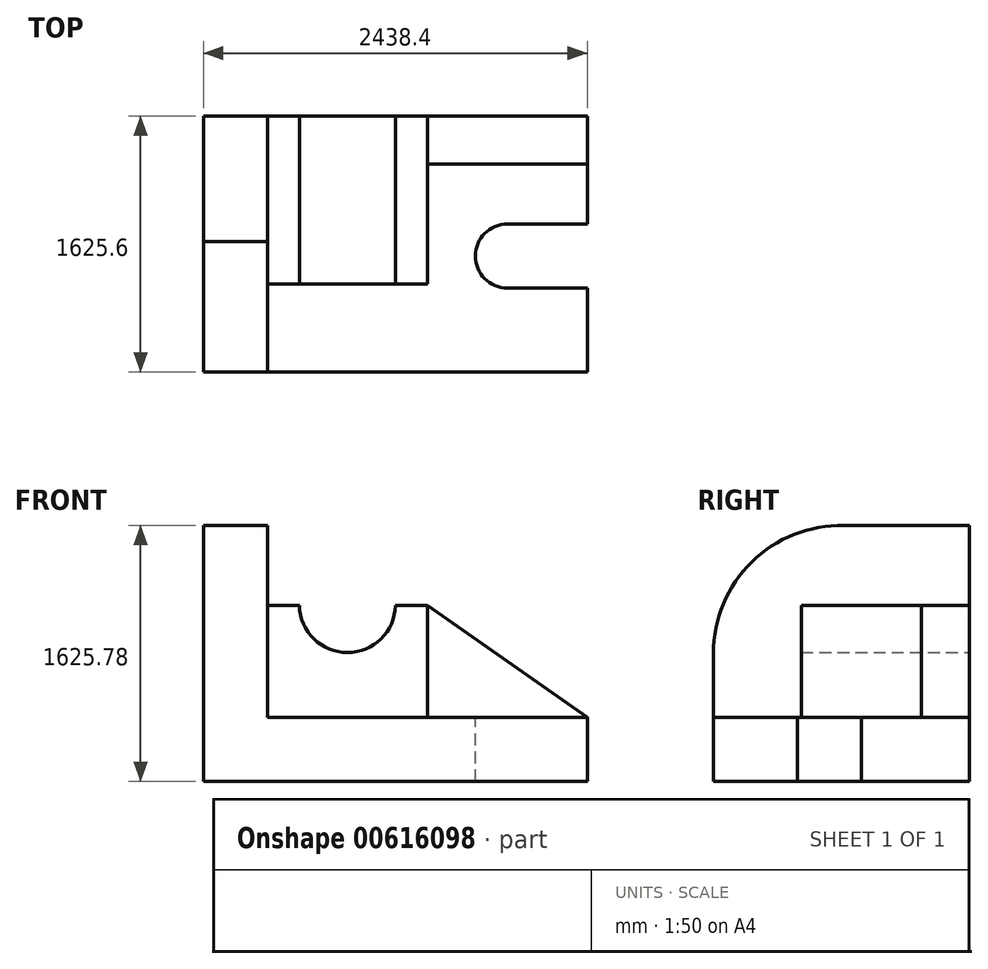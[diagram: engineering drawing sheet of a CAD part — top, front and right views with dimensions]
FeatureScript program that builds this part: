
annotation { "Feature Type Name" : "Feature", "Feature Type Description" : "" }
export const myFeature = defineFeature(function(context is Context, id is Id, definition is map)
    precondition{}
    {
        {
            var Q0;
            Q0=qCreatedBy(makeId("Top.planeOp"),FACE);
            var sketch = newSketch(context, id + "F0", { "sketchPlane" : qUnion([Q0])});
            skLineSegment(sketch, "E0.bottom", {"start": v(-2382.66, 1583.48) * mm, "end": v(55.74, 1583.48) * mm});
            skLineSegment(sketch, "E0.top", {"start": v(-2382.66, -42.12) * mm, "end": v(55.74, -42.12) * mm});
            skLineSegment(sketch, "E0.left", {"start": v(-2382.66, 1583.48) * mm, "end": v(-2382.66, -42.12) * mm});
            skLineSegment(sketch, "E0.right", {"start": v(55.74, 1583.48) * mm, "end": v(55.74, -42.12) * mm});
            skSolve(sketch);
        }
        {
            var Q0;
            Q0=makeQuery(id+"F0.imprint","IMPRINT",FACE,{"disambiguationData":[TD([[makeQuery(id+"F0.imprint","IMPRINT",EDGE,{"derivedFrom":sQuery(id+"F0.wireOp",EDGE,"E0.bottom")}),-1.0]])]});
            extrude(context, id + "F1", {"entities" : qUnion([Q0]), "depth" : 406.4 * mm, "offsetDistance" : 25.4 * mm});
        }
        {
            var Q0;
            Q0=makeQuery(id+"F1.opExtrude","SWEPT_FACE",FACE,{"disambiguationData":[OSD([sQuery(id+"F0.wireOp",EDGE,"E0.left")])]});
            var sketch = newSketch(context, id + "F2", { "sketchPlane" : qUnion([Q0])});
            skLineSegment(sketch, "E1", {"start": v(-1583.48, 0) * mm, "end": v(42.12, 0) * mm});
            skLineSegment(sketch, "E2", {"start": v(42.12, 0) * mm, "end": v(42.12, 812.98) * mm});
            skArc(sketch, "E3", {"start": v(42.12, 812.98) * mm, "mid": v(-202.01, 1393.72) * mm, "end": v(-787.76, 1625.6) * mm});
            skLineSegment(sketch, "E4", {"start": v(-787.76, 1625.6) * mm, "end": v(-1583.48, 1625.6) * mm});
            skLineSegment(sketch, "E5", {"start": v(-1583.48, 1625.6) * mm, "end": v(-1583.48, 0) * mm});
            skSolve(sketch);
        }
        {
            var Q0;
            {var subQ3=sQuery(id+"F2.wireOp",EDGE,"E3");Q0=makeQuery(id+"F2.imprint","IMPRINT",FACE,{"disambiguationData":[TD([[makeQuery(id+"F2.imprint","IMPRINT",EDGE,{"derivedFrom":subQ3}),1.0]])]});}
            extrude(context, id + "F3", {"entities" : qUnion([Q0]), "operationType" : NewBodyOperationType.ADD, "oppositeDirection" : true, "depth" : 406.4 * mm, "offsetDistance" : 25.4 * mm});
        }
        {
            var Q0;
            Q0=makeQuery(id+"F1.opExtrude","CAP_FACE",FACE,{"disambiguationData":[OSD([sQuery(id+"F0.wireOp",EDGE,"E0.bottom"),sQuery(id+"F0.wireOp",EDGE,"E0.top"),sQuery(id+"F0.wireOp",EDGE,"E0.left"),sQuery(id+"F0.wireOp",EDGE,"E0.right")])],"isStart":false});
            var sketch = newSketch(context, id + "F4", { "sketchPlane" : qUnion([Q0])});
            skLineSegment(sketch, "E6.bottom", {"start": v(-1976.26, 1583.48) * mm, "end": v(-960.26, 1583.48) * mm});
            skLineSegment(sketch, "E6.top", {"start": v(-1976.26, 516.68) * mm, "end": v(-960.26, 516.68) * mm});
            skLineSegment(sketch, "E6.left", {"start": v(-1976.26, 1583.48) * mm, "end": v(-1976.26, 516.68) * mm});
            skLineSegment(sketch, "E6.right", {"start": v(-960.26, 1583.48) * mm, "end": v(-960.26, 516.68) * mm});
            skSolve(sketch);
        }
        {
            var Q0;
            Q0=makeQuery(id+"F4.imprint","IMPRINT",FACE,{"disambiguationData":[TD([[makeQuery(id+"F4.imprint","IMPRINT",EDGE,{"derivedFrom":sQuery(id+"F4.wireOp",EDGE,"E6.bottom")}),-1.0]])]});
            extrude(context, id + "F5", {"entities" : qUnion([Q0]), "operationType" : NewBodyOperationType.ADD, "depth" : 711.2 * mm, "offsetDistance" : 25.4 * mm});
        }
        {
            var Q0;
            Q0=makeQuery(id+"F5.boolean.opBoolean","MERGE",FACE,{"derivedFrom":[makeQuery(id+"F3.boolean.opBoolean","MERGE",FACE,{"derivedFrom":[makeQuery(id+"F1.opExtrude","SWEPT_FACE",FACE,{"disambiguationData":[OSD([sQuery(id+"F0.wireOp",EDGE,"E0.bottom")])]}),makeQuery(id+"F3.opExtrude","SWEPT_FACE",FACE,{"disambiguationData":[OSD([sQuery(id+"F2.wireOp",EDGE,"E5")])]})]}),makeQuery(id+"F5.opExtrude","SWEPT_FACE",FACE,{"disambiguationData":[OSD([sQuery(id+"F4.wireOp",EDGE,"E6.bottom")])]})]});
            var sketch = newSketch(context, id + "F6", { "sketchPlane" : qUnion([Q0])});
            skLineSegment(sketch, "E7", {"start": v(-55.74, 406.4) * mm, "end": v(960.26, 1117.6) * mm});
            skLineSegment(sketch, "E8", {"start": v(960.26, 1117.6) * mm, "end": v(960.26, 0) * mm});
            skLineSegment(sketch, "E9", {"start": v(960.26, 0) * mm, "end": v(-55.74, 0) * mm});
            skLineSegment(sketch, "E10", {"start": v(-55.74, 0) * mm, "end": v(-55.74, 406.4) * mm});
            skSolve(sketch);
        }
        {
            var Q0;
            Q0 = qSketchRegion(id + "F6", true);
            extrude(context, id + "F7", {"entities" : qUnion([Q0]), "operationType" : NewBodyOperationType.ADD, "oppositeDirection" : true, "depth" : 304.8 * mm, "offsetDistance" : 25.4 * mm});
        }
        {
            var Q0;
            {var subQ7=makeQuery(id+"F5.opExtrude","CAP_EDGE",EDGE,{"disambiguationData":[OSD([sQuery(id+"F4.wireOp",EDGE,"E6.bottom")])],"isStart":false});Q0=makeQuery(id+"F6.imprint","IMPRINT",FACE,{"disambiguationData":[TD([[makeQuery(id+"F6.imprint","IMPRINT",EDGE,{"derivedFrom":subQ7}),1.0]])]});}
            var sketch = newSketch(context, id + "F8", { "sketchPlane" : qUnion([Q0])});
            skCircle(sketch, "E11", {"center": v(1468.23, 1123.64) * mm, "radius": 304.8 * mm});
            skSolve(sketch);
        }
        {
            var Q0;
            Q0 = qSketchRegion(id + "F8", true);
            extrude(context, id + "F9", {"entities" : qUnion([Q0]), "operationType" : NewBodyOperationType.REMOVE, "endBound" : BoundingType.THROUGH_ALL, "oppositeDirection" : true, "depth" : 25.4 * mm, "offsetDistance" : 25.4 * mm});
        }
        {
            var Q0;
            Q0=makeQuery(id+"F1.opExtrude","CAP_FACE",FACE,{"disambiguationData":[OSD([sQuery(id+"F0.wireOp",EDGE,"E0.bottom"),sQuery(id+"F0.wireOp",EDGE,"E0.top"),sQuery(id+"F0.wireOp",EDGE,"E0.left"),sQuery(id+"F0.wireOp",EDGE,"E0.right")])],"isStart":false});
            var sketch = newSketch(context, id + "F10", { "sketchPlane" : qUnion([Q0])});
            skLineSegment(sketch, "E12", {"start": v(55.74, 425.43) * mm, "end": v(55.74, 897.68) * mm});
            skPoint(sketch, "E12.endSnap0", {"position": v(-960.26, 897.68) * mm});
            skLineSegment(sketch, "E13", {"start": v(55.74, 897.68) * mm, "end": v(-452.26, 897.68) * mm});
            skArc(sketch, "E14", {"start": v(-452.26, 897.68) * mm, "mid": v(-655.46, 694.48) * mm, "end": v(-452.26, 491.28) * mm});
            skLineSegment(sketch, "E15", {"start": v(-452.26, 491.28) * mm, "end": v(55.74, 491.28) * mm});
            skLineSegment(sketch, "E16", {"start": v(55.74, 491.28) * mm, "end": v(55.74, 897.68) * mm});
            skSolve(sketch);
        }
        {
            var Q0;
            Q0=makeQuery(id+"F10.imprint","IMPRINT",FACE,{"disambiguationData":[TD([[makeQuery(id+"F10.imprint","IMPRINT",EDGE,{"derivedFrom":sQuery(id+"F10.wireOp",EDGE,"E13")}),1.0]])]});
            extrude(context, id + "F11", {"entities" : qUnion([Q0]), "operationType" : NewBodyOperationType.REMOVE, "endBound" : BoundingType.THROUGH_ALL, "oppositeDirection" : true, "depth" : 25.4 * mm, "offsetDistance" : 25.4 * mm});
        }
    });
